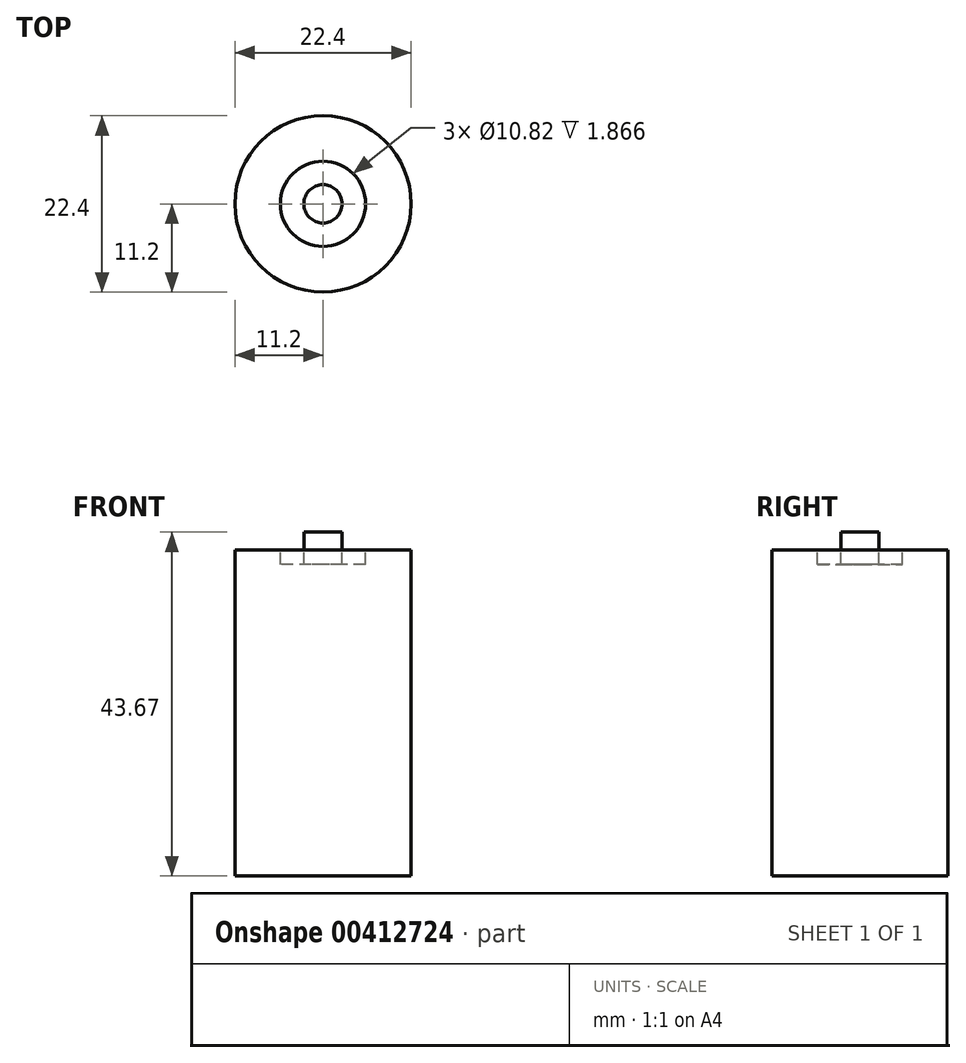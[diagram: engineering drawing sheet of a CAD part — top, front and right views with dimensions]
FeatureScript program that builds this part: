
annotation { "Feature Type Name" : "Feature", "Feature Type Description" : "" }
export const myFeature = defineFeature(function(context is Context, id is Id, definition is map)
    precondition{}
    {
        {
            var Q0;
            Q0=qCreatedBy(makeId("Front.planeOp"),FACE);
            var sketch = newSketch(context, id + "F0", { "sketchPlane" : qUnion([Q0])});
            skLineSegment(sketch, "E0", {"start": v(0, 0) * mm, "end": v(11.2, 0) * mm});
            skLineSegment(sketch, "E1", {"start": v(11.2, 0) * mm, "end": v(11.2, 41.43) * mm});
            skLineSegment(sketch, "E2", {"start": v(2.43, 41.43) * mm, "end": v(2.43, 43.67) * mm});
            skLineSegment(sketch, "E3", {"start": v(2.43, 43.67) * mm, "end": v(0, 43.67) * mm});
            skLineSegment(sketch, "E4", {"start": v(0, 43.67) * mm, "end": v(0, 0) * mm});
            skLineSegment(sketch, "E5", {"start": v(11.2, 41.43) * mm, "end": v(5.41, 41.43) * mm});
            skLineSegment(sketch, "E6", {"start": v(5.41, 41.43) * mm, "end": v(5.41, 39.56) * mm});
            skLineSegment(sketch, "E7", {"start": v(2.43, 41.43) * mm, "end": v(2.43, 39.56) * mm});
            skLineSegment(sketch, "E8", {"start": v(2.43, 39.56) * mm, "end": v(5.41, 39.56) * mm});
            skSolve(sketch);
        }
        {
            var Q0;
            Q0=makeQuery(id+"F0.imprint","IMPRINT",FACE,{"disambiguationData":[TD([[makeQuery(id+"F0.imprint","IMPRINT",EDGE,{"derivedFrom":sQuery(id+"F0.wireOp",EDGE,"E0")}),1.0]])]});
            var Q1;
            Q1=sQuery(id+"F0.wireOp",EDGE,"E4");
            revolve(context, id + "F1", {"entities" : qUnion([Q0]), "axis" : qUnion([Q1]), "revolveType" : RevolveType.FULL});
        }
    });
